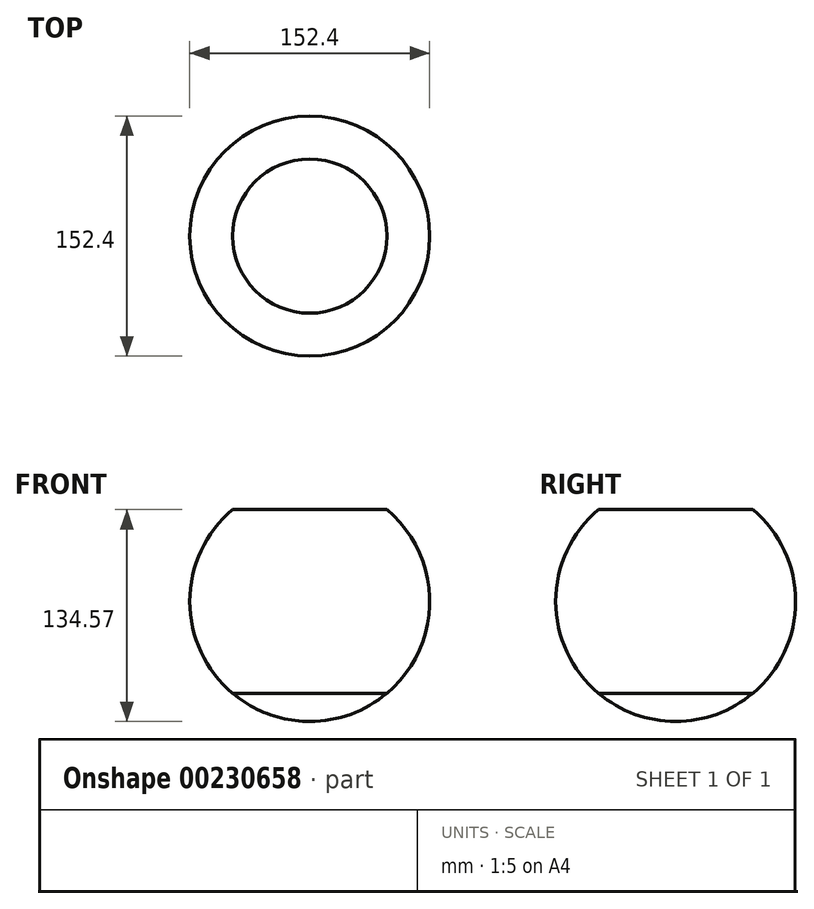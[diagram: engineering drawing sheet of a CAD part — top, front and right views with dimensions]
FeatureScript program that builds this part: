
annotation { "Feature Type Name" : "Feature", "Feature Type Description" : "" }
export const myFeature = defineFeature(function(context is Context, id is Id, definition is map)
    precondition{}
    {
        {
            var Q0;
            Q0=qCreatedBy(makeId("Front.planeOp"),FACE);
            var sketch = newSketch(context, id + "F0", { "sketchPlane" : qUnion([Q0])});
            skArc(sketch, "E0", {"start": v(0, -76.2) * mm, "mid": v(76.2, 0) * mm, "end": v(0, 76.2) * mm});
            skLineSegment(sketch, "E1", {"start": v(48.98, -58.37) * mm, "end": v(93.3, -21.18) * mm, "construction": true});
            skLineSegment(sketch, "E2", {"start": v(0, 76.2) * mm, "end": v(0, -76.2) * mm});
            skLineSegment(sketch, "E3", {"start": v(48.98, -58.37) * mm, "end": v(0, -58.37) * mm});
            skLineSegment(sketch, "E4", {"start": v(48.98, 58.37) * mm, "end": v(91.45, 22.73) * mm, "construction": true});
            skLineSegment(sketch, "E5", {"start": v(48.98, 58.37) * mm, "end": v(0, 58.37) * mm});
            skSolve(sketch);
        }
        {
            var Q0;
            {var subQ0=sQuery(id+"F0.wireOp",EDGE,"E3");Q0=makeQuery(id+"F0.imprint","IMPRINT",FACE,{"disambiguationData":[TD([[makeQuery(id+"F0.imprint","IMPRINT",EDGE,{"derivedFrom":subQ0}),-1.0]])]});}
            var Q1;
            Q1=sQuery(id+"F0.wireOp",EDGE,"E2");
            revolve(context, id + "F1", {"entities" : qUnion([Q0]), "axis" : qUnion([Q1]), "revolveType" : RevolveType.FULL});
        }
        {
            var Q0;
            {var subQ3=sQuery(id+"F0.wireOp",EDGE,"E3");Q0=makeQuery(id+"F0.imprint","IMPRINT",FACE,{"disambiguationData":[TD([[makeQuery(id+"F0.imprint","IMPRINT",EDGE,{"derivedFrom":subQ3}),1.0]])]});}
            var Q1;
            Q1=sQuery(id+"F0.wireOp",EDGE,"E2");
            revolve(context, id + "F2", {"entities" : qUnion([Q0]), "axis" : qUnion([Q1]), "revolveType" : RevolveType.FULL});
        }
    });
